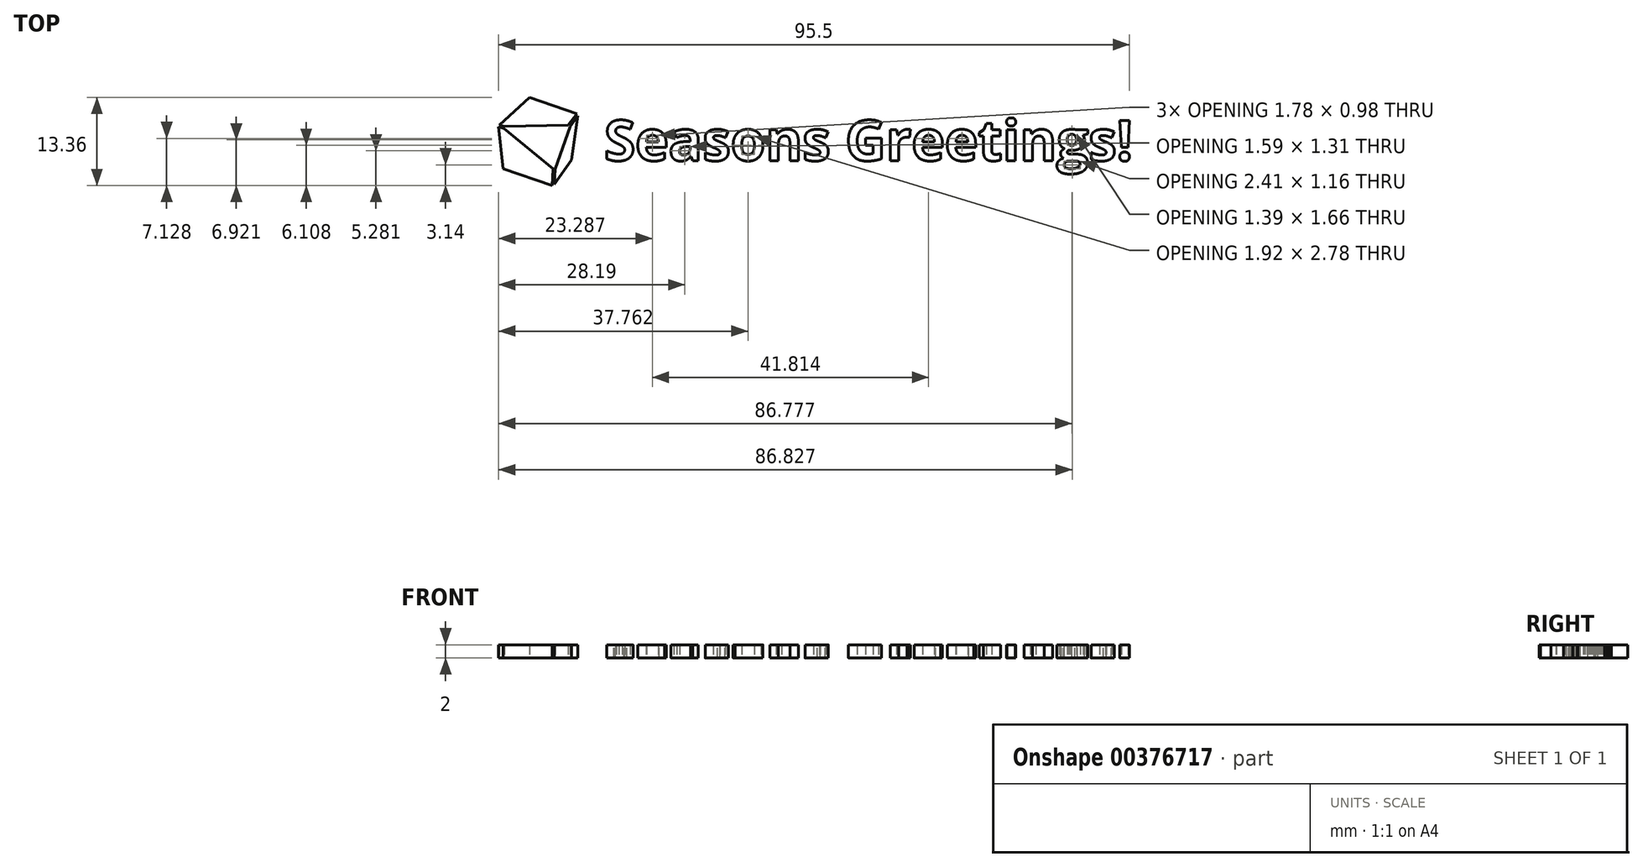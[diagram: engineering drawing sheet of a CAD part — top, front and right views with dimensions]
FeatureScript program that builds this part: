
annotation { "Feature Type Name" : "Feature", "Feature Type Description" : "" }
export const myFeature = defineFeature(function(context is Context, id is Id, definition is map)
    precondition{}
    {
        {
            var Q0;
            Q0=qCreatedBy(makeId("Top.planeOp"),FACE);
            var sketch = newSketch(context, id + "F0", { "sketchPlane" : qUnion([Q0])});
            skText(sketch, "E0", { "text": "Seasons Greetings!", "fontName": "OpenSans-Bold.ttf"});
            skLineSegment(sketch, "E1", {"start": v(-6, 2.2) * mm, "end": v(-5.18, 1.94) * mm});
            skLineSegment(sketch, "E2", {"start": v(-5.18, 1.94) * mm, "end": v(2.22, -4.16) * mm});
            skLineSegment(sketch, "E3", {"start": v(2.22, -4.16) * mm, "end": v(2.09, -6.68) * mm});
            skLineSegment(sketch, "E4", {"start": v(2.09, -6.68) * mm, "end": v(-5.3, -4.1) * mm});
            skLineSegment(sketch, "E5", {"start": v(-5.3, -4.1) * mm, "end": v(-6, 2.2) * mm});
            skLineSegment(sketch, "E6", {"start": v(6, 3.9) * mm, "end": v(4.82, 2.27) * mm});
            skLineSegment(sketch, "E7", {"start": v(4.82, 2.27) * mm, "end": v(2.6, -4.19) * mm});
            skLineSegment(sketch, "E8", {"start": v(2.6, -4.19) * mm, "end": v(2.46, -6.51) * mm});
            skLineSegment(sketch, "E9", {"start": v(2.46, -6.51) * mm, "end": v(5.04, -2.82) * mm});
            skLineSegment(sketch, "E10", {"start": v(5.04, -2.82) * mm, "end": v(6, 3.9) * mm});
            skLineSegment(sketch, "E11", {"start": v(4.56, 2.49) * mm, "end": v(5.83, 4.2) * mm});
            skLineSegment(sketch, "E12", {"start": v(5.83, 4.2) * mm, "end": v(-1.3, 6.68) * mm});
            skLineSegment(sketch, "E13", {"start": v(-1.3, 6.68) * mm, "end": v(-5.86, 2.49) * mm});
            skLineSegment(sketch, "E14", {"start": v(-5.86, 2.49) * mm, "end": v(-5.1, 2.26) * mm});
            skLineSegment(sketch, "E15", {"start": v(-5.1, 2.26) * mm, "end": v(4.56, 2.49) * mm});
            const initialGuessF0  = {"E0": [0.01, -0.0029, 1, 0, 0.00614]};
            skSetInitialGuess(sketch, initialGuessF0);
            skSolve(sketch);
        }
        {
            var Q0;
            Q0 = qSketchRegion(id + "F0", true);
            extrude(context, id + "F1", {"entities" : qUnion([Q0]), "depth" : 2 * mm});
        }
    });
